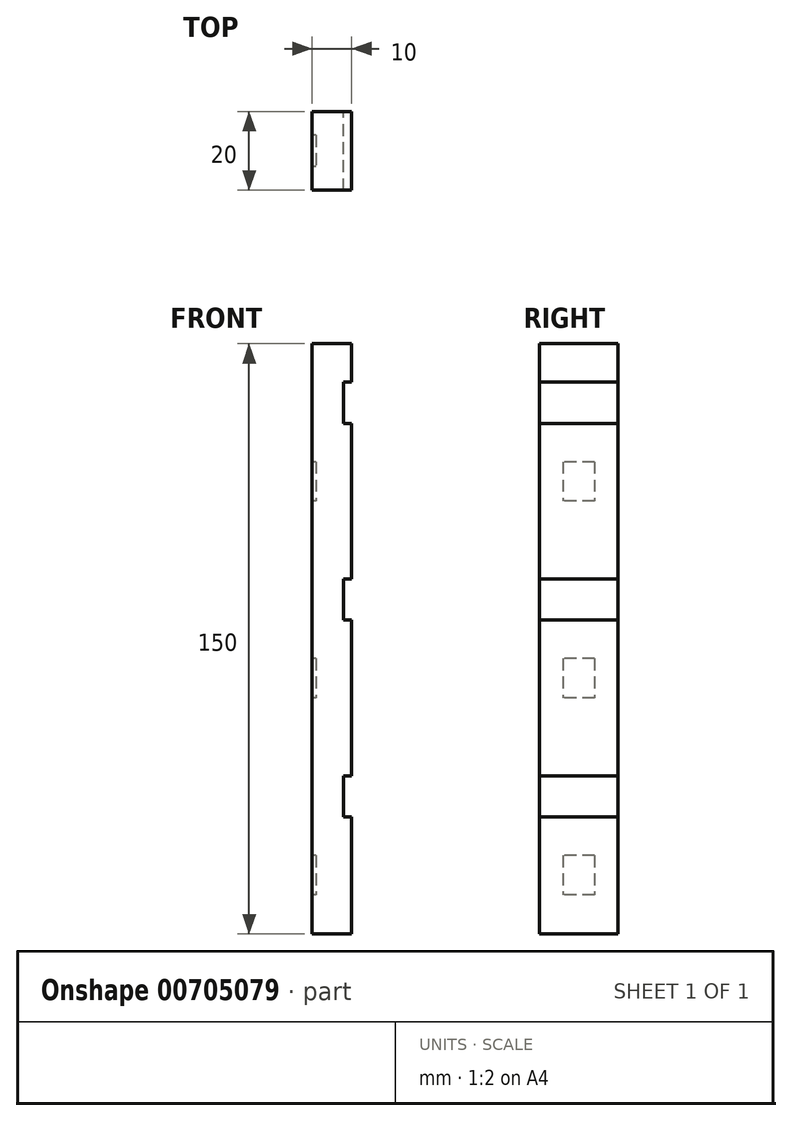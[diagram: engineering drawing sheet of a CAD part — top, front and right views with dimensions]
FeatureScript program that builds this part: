
annotation { "Feature Type Name" : "Feature", "Feature Type Description" : "" }
export const myFeature = defineFeature(function(context is Context, id is Id, definition is map)
    precondition{}
    {
        {
            var Q0;
            Q0=qCreatedBy(makeId("Top.planeOp"),FACE);
            var sketch = newSketch(context, id + "F0", { "sketchPlane" : qUnion([Q0])});
            skLineSegment(sketch, "E0.bottom", {"start": v(0, 0) * mm, "end": v(8, 0) * mm});
            skLineSegment(sketch, "E0.top", {"start": v(0, 20) * mm, "end": v(8, 20) * mm});
            skLineSegment(sketch, "E0.left", {"start": v(0, 0) * mm, "end": v(0, 20) * mm});
            skLineSegment(sketch, "E0.right", {"start": v(8, 0) * mm, "end": v(8, 20) * mm});
            skSolve(sketch);
        }
        {
            var Q0;
            Q0 = qSketchRegion(id + "F0", true);
            extrude(context, id + "F1", {"entities" : qUnion([Q0]), "depth" : 150 * mm, "offsetDistance" : 25 * mm});
        }
        {
            var Q0;
            Q0=makeQuery(id+"F1.opExtrude","SWEPT_FACE",FACE,{"disambiguationData":[OSD([sQuery(id+"F0.wireOp",EDGE,"E0.right")])]});
            var sketch = newSketch(context, id + "F2", { "sketchPlane" : qUnion([Q0])});
            skLineSegment(sketch, "E1.bottom", {"start": v(0, 150) * mm, "end": v(20, 150) * mm});
            skLineSegment(sketch, "E1.top", {"start": v(0, 140.25) * mm, "end": v(20, 140.25) * mm});
            skLineSegment(sketch, "E1.left", {"start": v(0, 150) * mm, "end": v(0, 140.25) * mm});
            skLineSegment(sketch, "E1.right", {"start": v(20, 150) * mm, "end": v(20, 140.25) * mm});
            skLineSegment(sketch, "E2.bottom", {"start": v(0, 129.75) * mm, "end": v(20, 129.75) * mm});
            skLineSegment(sketch, "E2.top", {"start": v(0, 90.25) * mm, "end": v(20, 90.25) * mm});
            skLineSegment(sketch, "E2.left", {"start": v(0, 129.75) * mm, "end": v(0, 90.25) * mm});
            skLineSegment(sketch, "E2.right", {"start": v(20, 129.75) * mm, "end": v(20, 90.25) * mm});
            skLineSegment(sketch, "E3.bottom", {"start": v(0, 79.75) * mm, "end": v(20, 79.75) * mm});
            skLineSegment(sketch, "E3.top", {"start": v(0, 40.25) * mm, "end": v(20, 40.25) * mm});
            skLineSegment(sketch, "E3.left", {"start": v(0, 79.75) * mm, "end": v(0, 40.25) * mm});
            skLineSegment(sketch, "E3.right", {"start": v(20, 79.75) * mm, "end": v(20, 40.25) * mm});
            skLineSegment(sketch, "E4.bottom", {"start": v(0, 0) * mm, "end": v(20, 0) * mm});
            skLineSegment(sketch, "E4.top", {"start": v(0, 29.75) * mm, "end": v(20, 29.75) * mm});
            skLineSegment(sketch, "E4.left", {"start": v(0, 0) * mm, "end": v(0, 29.75) * mm});
            skLineSegment(sketch, "E4.right", {"start": v(20, 0) * mm, "end": v(20, 29.75) * mm});
            skSolve(sketch);
        }
        {
            var Q0;
            Q0 = qSketchRegion(id + "F2", true);
            extrude(context, id + "F3", {"entities" : qUnion([Q0]), "operationType" : NewBodyOperationType.ADD, "depth" : 2 * mm, "offsetDistance" : 25 * mm});
        }
        {
            var Q0;
            Q0=makeQuery(id+"F1.opExtrude","SWEPT_FACE",FACE,{"disambiguationData":[OSD([sQuery(id+"F0.wireOp",EDGE,"E0.left")])]});
            var sketch = newSketch(context, id + "F4", { "sketchPlane" : qUnion([Q0])});
            skLineSegment(sketch, "E5.bottom", {"start": v(-14, 120) * mm, "end": v(-6, 120) * mm});
            skLineSegment(sketch, "E5.top", {"start": v(-14, 110) * mm, "end": v(-6, 110) * mm});
            skLineSegment(sketch, "E5.left", {"start": v(-14, 120) * mm, "end": v(-14, 110) * mm});
            skLineSegment(sketch, "E5.right", {"start": v(-6, 120) * mm, "end": v(-6, 110) * mm});
            skLineSegment(sketch, "E6.bottom", {"start": v(-14, 70) * mm, "end": v(-6, 70) * mm});
            skLineSegment(sketch, "E6.top", {"start": v(-14, 60) * mm, "end": v(-6, 60) * mm});
            skLineSegment(sketch, "E6.left", {"start": v(-14, 70) * mm, "end": v(-14, 60) * mm});
            skLineSegment(sketch, "E6.right", {"start": v(-6, 70) * mm, "end": v(-6, 60) * mm});
            skLineSegment(sketch, "E7.bottom", {"start": v(-14, 20) * mm, "end": v(-6, 20) * mm});
            skLineSegment(sketch, "E7.top", {"start": v(-14, 10) * mm, "end": v(-6, 10) * mm});
            skLineSegment(sketch, "E7.left", {"start": v(-14, 20) * mm, "end": v(-14, 10) * mm});
            skLineSegment(sketch, "E7.right", {"start": v(-6, 20) * mm, "end": v(-6, 10) * mm});
            skSolve(sketch);
        }
        {
            var Q0;
            Q0 = qSketchRegion(id + "F4", true);
            extrude(context, id + "F5", {"entities" : qUnion([Q0]), "operationType" : NewBodyOperationType.REMOVE, "oppositeDirection" : true, "depth" : 1 * mm, "offsetDistance" : 25 * mm});
        }
    });
